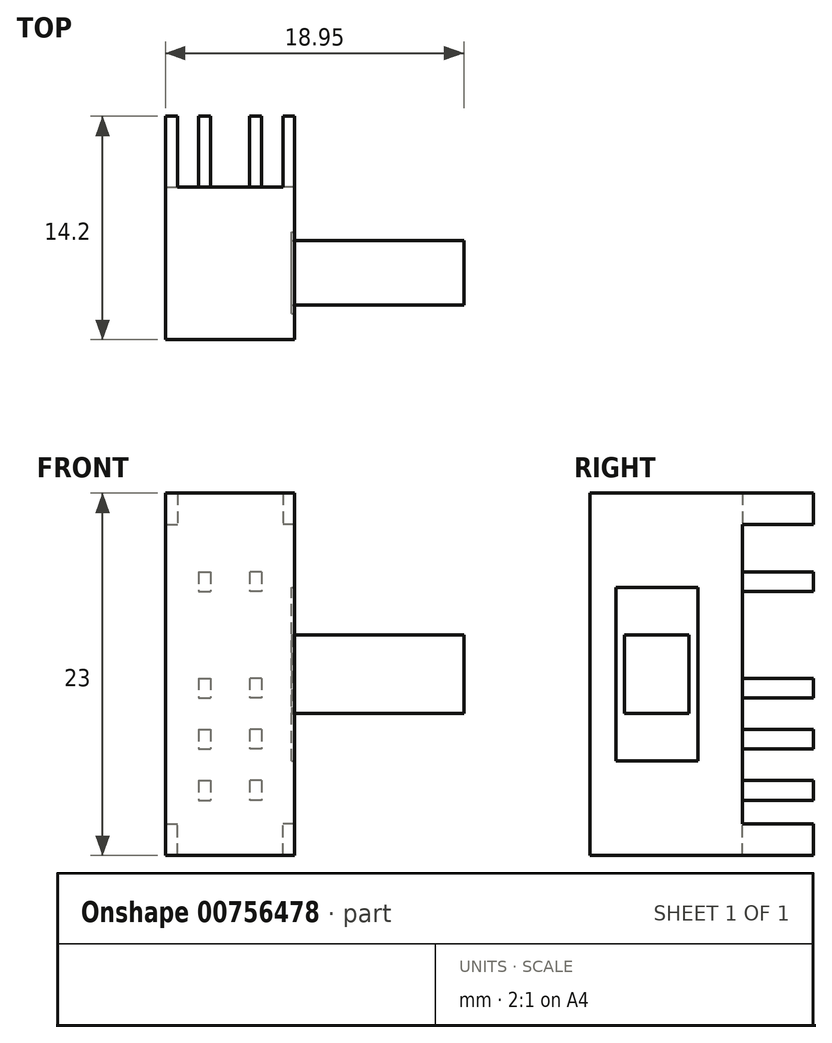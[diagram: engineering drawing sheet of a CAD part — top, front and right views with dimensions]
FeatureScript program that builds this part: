
annotation { "Feature Type Name" : "Feature", "Feature Type Description" : "" }
export const myFeature = defineFeature(function(context is Context, id is Id, definition is map)
    precondition{}
    {
        {
            var Q0;
            Q0=qCreatedBy(makeId("Front.planeOp"),FACE);
            var sketch = newSketch(context, id + "F0", { "sketchPlane" : qUnion([Q0])});
            skLineSegment(sketch, "E0.bottom", {"start": v(-4.1, -11.5) * mm, "end": v(4.1, -11.5) * mm});
            skLineSegment(sketch, "E0.top", {"start": v(-4.1, 11.5) * mm, "end": v(4.1, 11.5) * mm});
            skLineSegment(sketch, "E0.left", {"start": v(-4.1, -11.5) * mm, "end": v(-4.1, 11.5) * mm});
            skLineSegment(sketch, "E0.right", {"start": v(4.1, -11.5) * mm, "end": v(4.1, 11.5) * mm});
            skPoint(sketch, "E0.middle", {"position": v(0, 0) * mm});
            skSolve(sketch);
        }
        {
            var Q0;
            Q0=makeQuery(id+"F0.imprint","IMPRINT",FACE,{"disambiguationData":[TD([[makeQuery(id+"F0.imprint","IMPRINT",EDGE,{"derivedFrom":sQuery(id+"F0.wireOp",EDGE,"E0.bottom")}),1.0]])]});
            extrude(context, id + "F1", {"entities" : qUnion([Q0]), "depth" : 9.7 * mm, "offsetDistance" : 25 * mm});
        }
        {
            var Q0;
            Q0=makeQuery(id+"F1.opExtrude","SWEPT_FACE",FACE,{"disambiguationData":[OSD([sQuery(id+"F0.wireOp",EDGE,"E0.right")])]});
            var sketch = newSketch(context, id + "F2", { "sketchPlane" : qUnion([Q0])});
            skLineSegment(sketch, "E1.0", {"start": v(-9.7, -11.5) * mm, "end": v(-9.7, 11.5) * mm});
            skLineSegment(sketch, "E1.1", {"start": v(-9.7, 11.5) * mm, "end": v(0, 11.5) * mm});
            skLineSegment(sketch, "E1.2", {"start": v(0, -11.5) * mm, "end": v(0, 11.5) * mm});
            skLineSegment(sketch, "E1.3", {"start": v(-9.7, -11.5) * mm, "end": v(0, -11.5) * mm});
            skLineSegment(sketch, "E2", {"start": v(-7.5, 2.5) * mm, "end": v(-7.5, -2.5) * mm});
            skLineSegment(sketch, "E3", {"start": v(0, 0) * mm, "end": v(-9.7, 0) * mm, "construction": true});
            skLineSegment(sketch, "E4", {"start": v(-3.4, 2.5) * mm, "end": v(-3.4, -2.5) * mm});
            skLineSegment(sketch, "E5", {"start": v(-7.5, 2.5) * mm, "end": v(-3.4, 2.5) * mm});
            skLineSegment(sketch, "E6", {"start": v(-7.5, -2.5) * mm, "end": v(-3.4, -2.5) * mm});
            skLineSegment(sketch, "E7", {"start": v(-5.45, 2.5) * mm, "end": v(-5.45, -2.5) * mm, "construction": true});
            skLineSegment(sketch, "E8.bottom", {"start": v(-8.05, -5.5) * mm, "end": v(-2.85, -5.5) * mm});
            skLineSegment(sketch, "E8.top", {"start": v(-8.05, 5.5) * mm, "end": v(-2.85, 5.5) * mm});
            skLineSegment(sketch, "E8.left", {"start": v(-8.05, -5.5) * mm, "end": v(-8.05, 5.5) * mm});
            skLineSegment(sketch, "E8.right", {"start": v(-2.85, -5.5) * mm, "end": v(-2.85, 5.5) * mm});
            skPoint(sketch, "E8.middle", {"position": v(-5.45, 0) * mm});
            skSolve(sketch);
        }
        {
            var Q0;
            Q0=makeQuery(id+"F2.imprint","IMPRINT",FACE,{"disambiguationData":[TD([[makeQuery(id+"F2.imprint","IMPRINT",EDGE,{"derivedFrom":sQuery(id+"F2.wireOp",EDGE,"E2")}),-1.0]])]});
            extrude(context, id + "F3", {"entities" : qUnion([Q0]), "operationType" : NewBodyOperationType.REMOVE, "oppositeDirection" : true, "depth" : .2 * mm, "offsetDistance" : 25 * mm});
        }
        {
            var Q0;
            Q0=makeQuery(id+"F3.boolean.opBoolean","SPLIT",FACE,{"disambiguationData":[TD([makeQuery(id+"F3.opExtrude","SWEPT_FACE",FACE,{"disambiguationData":[OSD([sQuery(id+"F2.wireOp",EDGE,"E2")])]})])],"derivedFrom":makeQuery(id+"F1.opExtrude","SWEPT_FACE",FACE,{"disambiguationData":[OSD([sQuery(id+"F0.wireOp",EDGE,"E0.right")])]})});
            extrude(context, id + "F4", {"entities" : qUnion([Q0]), "operationType" : NewBodyOperationType.ADD, "depth" : 10.75 * mm, "offsetDistance" : 25 * mm});
        }
        {
            var Q0;
            Q0=makeQuery(id+"F1.opExtrude","CAP_FACE",FACE,{"disambiguationData":[OSD([sQuery(id+"F0.wireOp",EDGE,"E0.bottom"),sQuery(id+"F0.wireOp",EDGE,"E0.top"),sQuery(id+"F0.wireOp",EDGE,"E0.left"),sQuery(id+"F0.wireOp",EDGE,"E0.right")])],"isStart":true});
            var sketch = newSketch(context, id + "F5", { "sketchPlane" : qUnion([Q0])});
            skLineSegment(sketch, "E9", {"start": v(-3.35, 11.5) * mm, "end": v(-3.35, 9.5) * mm});
            skLineSegment(sketch, "E10", {"start": v(0, 11.5) * mm, "end": v(0, -11.5) * mm, "construction": true});
            skLineSegment(sketch, "E11", {"start": v(-4.1, 0) * mm, "end": v(-2, 0) * mm, "construction": true});
            skLineSegment(sketch, "E12", {"start": v(-4.1, 9.5) * mm, "end": v(-3.35, 9.5) * mm});
            skLineSegment(sketch, "E13.MirrorCS", {"start": v(3.35, 11.5) * mm, "end": v(3.35, 9.5) * mm});
            skLineSegment(sketch, "E14.MirrorCS", {"start": v(4.1, 9.5) * mm, "end": v(3.35, 9.5) * mm});
            skLineSegment(sketch, "E15.MirrorCS", {"start": v(4.1, -9.5) * mm, "end": v(3.35, -9.5) * mm});
            skLineSegment(sketch, "E16.MirrorCS", {"start": v(3.35, -11.5) * mm, "end": v(3.35, -9.5) * mm});
            skLineSegment(sketch, "E17.MirrorCS", {"start": v(-4.1, -9.5) * mm, "end": v(-3.35, -9.5) * mm});
            skLineSegment(sketch, "E18.MirrorCS", {"start": v(-3.35, -11.5) * mm, "end": v(-3.35, -9.5) * mm});
            skLineSegment(sketch, "E19", {"start": v(-2, 6.5) * mm, "end": v(-2, 5.25) * mm});
            skLineSegment(sketch, "E20", {"start": v(-1.25, 6.5) * mm, "end": v(-1.25, 5.25) * mm});
            skLineSegment(sketch, "E21", {"start": v(-2, -0.25) * mm, "end": v(-1.25, -0.25) * mm});
            skLineSegment(sketch, "E22", {"start": v(-2, -1.5) * mm, "end": v(-1.25, -1.5) * mm});
            skLineSegment(sketch, "E23", {"start": v(-2, -3.5) * mm, "end": v(-1.25, -3.5) * mm});
            skLineSegment(sketch, "E24", {"start": v(-2, -4.75) * mm, "end": v(-1.25, -4.75) * mm});
            skLineSegment(sketch, "E25", {"start": v(-2, -6.75) * mm, "end": v(-1.25, -6.75) * mm});
            skLineSegment(sketch, "E26", {"start": v(-2, -8) * mm, "end": v(-1.25, -8) * mm});
            skPoint(sketch, "E27.orphan", {"position": v(-2, -11.5) * mm});
            skPoint(sketch, "E28.orphan", {"position": v(-1.25, -11.5) * mm});
            skLineSegment(sketch, "E29.trimOffspring", {"start": v(-1.25, -6.75) * mm, "end": v(-1.25, -8) * mm});
            skLineSegment(sketch, "E30.trimOffspring", {"start": v(-2, -6.75) * mm, "end": v(-2, -8) * mm});
            skLineSegment(sketch, "E31.trimOffspring", {"start": v(-1.25, -3.5) * mm, "end": v(-1.25, -4.75) * mm});
            skLineSegment(sketch, "E32.trimOffspring", {"start": v(-2, -3.5) * mm, "end": v(-2, -4.75) * mm});
            skLineSegment(sketch, "E33.trimOffspring", {"start": v(-1.25, -0.25) * mm, "end": v(-1.25, -1.5) * mm});
            skLineSegment(sketch, "E34.trimOffspring", {"start": v(-2, -0.25) * mm, "end": v(-2, -1.5) * mm});
            skLineSegment(sketch, "E35.trimOffspring", {"start": v(-1.25, 0) * mm, "end": v(4.1, 0) * mm, "construction": true});
            skLineSegment(sketch, "E36", {"start": v(-2, 6.5) * mm, "end": v(-1.25, 6.5) * mm});
            skLineSegment(sketch, "E37", {"start": v(-2, 5.25) * mm, "end": v(-1.25, 5.25) * mm});
            skPoint(sketch, "E38.orphan", {"position": v(-1.25, 11.5) * mm});
            skPoint(sketch, "E39.orphan", {"position": v(-2, 11.5) * mm});
            skLineSegment(sketch, "E40.MirrorCS", {"start": v(2, 6.5) * mm, "end": v(1.25, 6.5) * mm});
            skLineSegment(sketch, "E41.MirrorCS", {"start": v(1.25, 6.5) * mm, "end": v(1.25, 5.25) * mm});
            skLineSegment(sketch, "E42.MirrorCS", {"start": v(2, 5.25) * mm, "end": v(1.25, 5.25) * mm});
            skLineSegment(sketch, "E43.MirrorCS", {"start": v(2, 6.5) * mm, "end": v(2, 5.25) * mm});
            skLineSegment(sketch, "E44.MirrorCS", {"start": v(1.25, -0.25) * mm, "end": v(1.25, -1.5) * mm});
            skLineSegment(sketch, "E45.MirrorCS", {"start": v(2, -0.25) * mm, "end": v(2, -1.5) * mm});
            skLineSegment(sketch, "E46.MirrorCS", {"start": v(2, -0.25) * mm, "end": v(1.25, -0.25) * mm});
            skLineSegment(sketch, "E47.MirrorCS", {"start": v(2, -1.5) * mm, "end": v(1.25, -1.5) * mm});
            skLineSegment(sketch, "E48.MirrorCS", {"start": v(2, -3.5) * mm, "end": v(1.25, -3.5) * mm});
            skLineSegment(sketch, "E49.MirrorCS", {"start": v(2, -3.5) * mm, "end": v(2, -4.75) * mm});
            skLineSegment(sketch, "E50.MirrorCS", {"start": v(1.25, -3.5) * mm, "end": v(1.25, -4.75) * mm});
            skLineSegment(sketch, "E51.MirrorCS", {"start": v(2, -4.75) * mm, "end": v(1.25, -4.75) * mm});
            skLineSegment(sketch, "E52.MirrorCS", {"start": v(2, -6.75) * mm, "end": v(1.25, -6.75) * mm});
            skLineSegment(sketch, "E53.MirrorCS", {"start": v(1.25, -6.75) * mm, "end": v(1.25, -8) * mm});
            skLineSegment(sketch, "E54.MirrorCS", {"start": v(2, -6.75) * mm, "end": v(2, -8) * mm});
            skLineSegment(sketch, "E55.MirrorCS", {"start": v(2, -8) * mm, "end": v(1.25, -8) * mm});
            skSolve(sketch);
        }
        {
            var Q0;
            {var subQ0=sQuery(id+"F5.wireOp",EDGE,"E9");Q0=makeQuery(id+"F5.imprint","IMPRINT",FACE,{"disambiguationData":[TD([[makeQuery(id+"F5.imprint","IMPRINT",EDGE,{"derivedFrom":subQ0}),-1.0]])]});}
            var Q1;
            {var subQ0=sQuery(id+"F5.wireOp",EDGE,"E13.MirrorCS");Q1=makeQuery(id+"F5.imprint","IMPRINT",FACE,{"disambiguationData":[TD([[makeQuery(id+"F5.imprint","IMPRINT",EDGE,{"derivedFrom":subQ0}),1.0]])]});}
            var Q2;
            {var subQ0=sQuery(id+"F5.wireOp",EDGE,"E15.MirrorCS");Q2=makeQuery(id+"F5.imprint","IMPRINT",FACE,{"disambiguationData":[TD([[makeQuery(id+"F5.imprint","IMPRINT",EDGE,{"derivedFrom":subQ0}),1.0]])]});}
            var Q3;
            {var subQ0=sQuery(id+"F5.wireOp",EDGE,"E17.MirrorCS");Q3=makeQuery(id+"F5.imprint","IMPRINT",FACE,{"disambiguationData":[TD([[makeQuery(id+"F5.imprint","IMPRINT",EDGE,{"derivedFrom":subQ0}),-1.0]])]});}
            var Q4;
            Q4=makeQuery(id+"F5.imprint","IMPRINT",FACE,{"disambiguationData":[TD([[makeQuery(id+"F5.imprint","IMPRINT",EDGE,{"derivedFrom":sQuery(id+"F5.wireOp",EDGE,"E25")}),-1.0]])]});
            var Q5;
            Q5=makeQuery(id+"F5.imprint","IMPRINT",FACE,{"disambiguationData":[TD([[makeQuery(id+"F5.imprint","IMPRINT",EDGE,{"derivedFrom":sQuery(id+"F5.wireOp",EDGE,"E52.MirrorCS")}),1.0]])]});
            var Q6;
            Q6=makeQuery(id+"F5.imprint","IMPRINT",FACE,{"disambiguationData":[TD([[makeQuery(id+"F5.imprint","IMPRINT",EDGE,{"derivedFrom":sQuery(id+"F5.wireOp",EDGE,"E48.MirrorCS")}),1.0]])]});
            var Q7;
            Q7=makeQuery(id+"F5.imprint","IMPRINT",FACE,{"disambiguationData":[TD([[makeQuery(id+"F5.imprint","IMPRINT",EDGE,{"derivedFrom":sQuery(id+"F5.wireOp",EDGE,"E23")}),-1.0]])]});
            var Q8;
            Q8=makeQuery(id+"F5.imprint","IMPRINT",FACE,{"disambiguationData":[TD([[makeQuery(id+"F5.imprint","IMPRINT",EDGE,{"derivedFrom":sQuery(id+"F5.wireOp",EDGE,"E21")}),-1.0]])]});
            var Q9;
            Q9=makeQuery(id+"F5.imprint","IMPRINT",FACE,{"disambiguationData":[TD([[makeQuery(id+"F5.imprint","IMPRINT",EDGE,{"derivedFrom":sQuery(id+"F5.wireOp",EDGE,"E44.MirrorCS")}),1.0]])]});
            var Q10;
            Q10=makeQuery(id+"F5.imprint","IMPRINT",FACE,{"disambiguationData":[TD([[makeQuery(id+"F5.imprint","IMPRINT",EDGE,{"derivedFrom":sQuery(id+"F5.wireOp",EDGE,"E40.MirrorCS")}),1.0]])]});
            var Q11;
            Q11=makeQuery(id+"F5.imprint","IMPRINT",FACE,{"disambiguationData":[TD([[makeQuery(id+"F5.imprint","IMPRINT",EDGE,{"derivedFrom":sQuery(id+"F5.wireOp",EDGE,"E19")}),1.0]])]});
            extrude(context, id + "F6", {"entities" : qUnion([Q0, Q1, Q2, Q3, Q4, Q5, Q6, Q7, Q8, Q9, Q10, Q11]), "operationType" : NewBodyOperationType.ADD, "depth" : 4.5 * mm, "offsetDistance" : 25 * mm});
        }
    });
